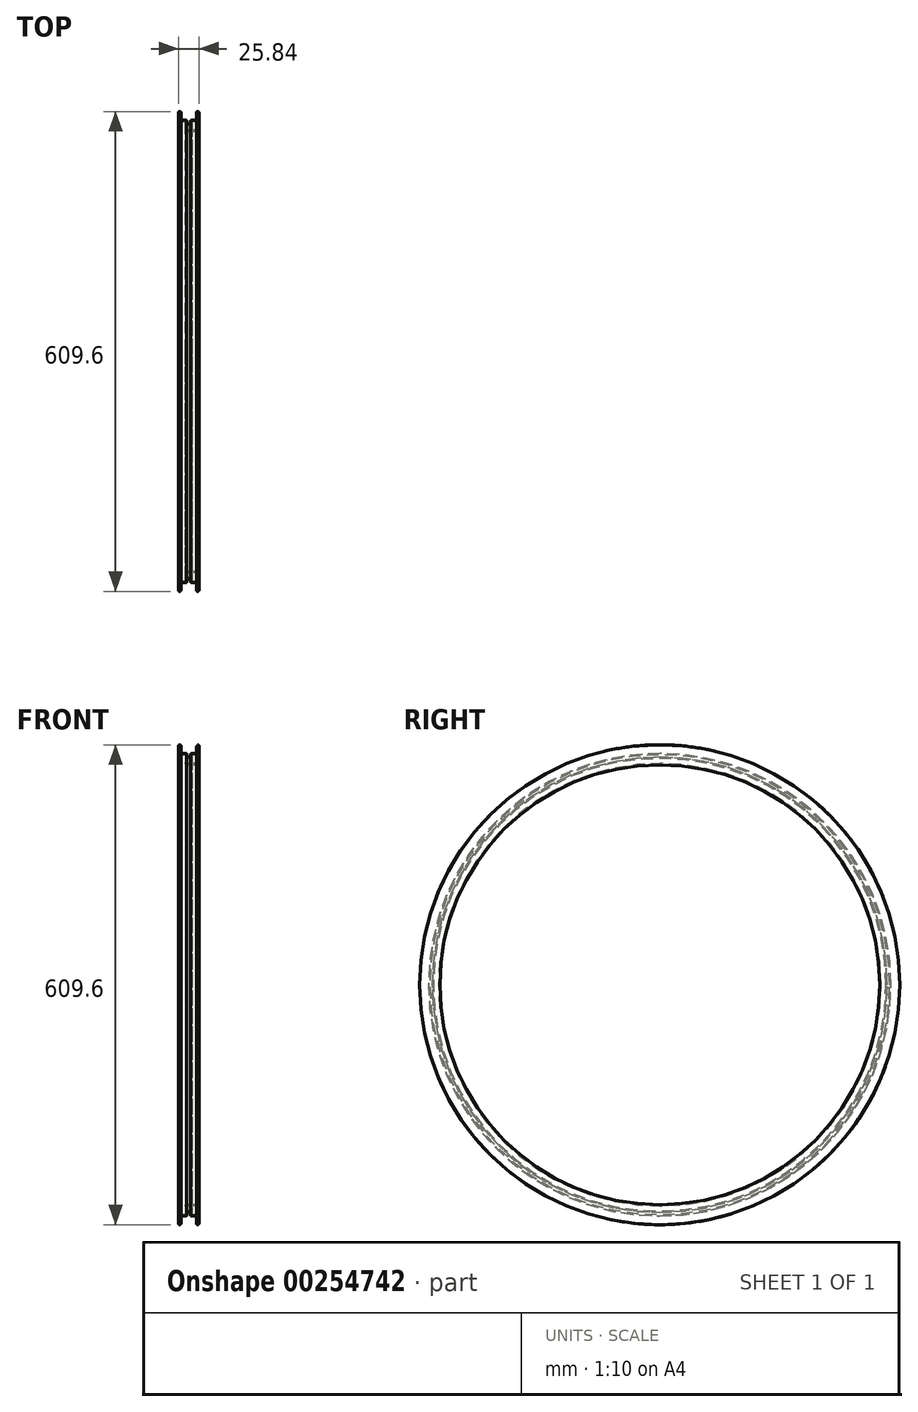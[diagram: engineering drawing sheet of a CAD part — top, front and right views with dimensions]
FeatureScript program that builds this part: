
annotation { "Feature Type Name" : "Feature", "Feature Type Description" : "" }
export const myFeature = defineFeature(function(context is Context, id is Id, definition is map)
    precondition{}
    {
        {
            var Q0;
            Q0=qCreatedBy(makeId("Front.planeOp"),FACE);
            var sketch = newSketch(context, id + "F0", { "sketchPlane" : qUnion([Q0])});
            skLineSegment(sketch, "E0", {"start": v(0, 0) * mm, "end": v(0, 140.25) * mm});
            skLineSegment(sketch, "E1", {"start": v(0, 279.4) * mm, "end": v(10.2, 279.4) * mm});
            skLineSegment(sketch, "E2", {"start": v(0, 280.92) * mm, "end": v(9.48, 280.92) * mm});
            skLineSegment(sketch, "E3", {"start": v(11.5, 304.8) * mm, "end": v(11.5, 304.8) * mm});
            skArc(sketch, "E4", {"start": v(9.48, 280.92) * mm, "mid": v(9.74, 281.03) * mm, "end": v(9.86, 281.28) * mm});
            skArc(sketch, "E5.trimOffspring", {"start": v(10.2, 279.4) * mm, "mid": v(10.97, 279.7) * mm, "end": v(11.33, 280.46) * mm});
            skArc(sketch, "E6", {"start": v(12.92, 303.17) * mm, "mid": v(10.53, 304.53) * mm, "end": v(10.97, 301.82) * mm});
            skLineSegment(sketch, "E7.trimOffspring", {"start": v(12.92, 303.17) * mm, "end": v(11.33, 280.46) * mm});
            skArc(sketch, "E8", {"start": v(11.27, 301.38) * mm, "mid": v(11.2, 301.65) * mm, "end": v(10.97, 301.82) * mm});
            skLineSegment(sketch, "E9.trimOffspring", {"start": v(11.27, 301.38) * mm, "end": v(9.86, 281.28) * mm});
            skLineSegment(sketch, "E10.trimOffspring", {"start": v(11.4, 304.8) * mm, "end": v(11.5, 304.8) * mm});
            skLineSegment(sketch, "E11.trimOffspring", {"start": v(0, 140.25) * mm, "end": v(-5.92, 55.63) * mm});
            skLineSegment(sketch, "E12.trimOffspring", {"start": v(0, 118.4) * mm, "end": v(-11.62, -47.77) * mm});
            skArc(sketch, "E13.MirrorCS", {"start": v(-12.92, 303.17) * mm, "mid": v(-10.53, 304.53) * mm, "end": v(-10.97, 301.82) * mm});
            skLineSegment(sketch, "E14.MirrorCS", {"start": v(-11.27, 301.38) * mm, "end": v(-9.86, 281.28) * mm});
            skLineSegment(sketch, "E15.MirrorCS", {"start": v(-12.92, 303.17) * mm, "end": v(-11.33, 280.46) * mm});
            skArc(sketch, "E16.MirrorCS", {"start": v(-11.27, 301.38) * mm, "mid": v(-11.2, 301.65) * mm, "end": v(-10.97, 301.82) * mm});
            skArc(sketch, "E17.MirrorCS", {"start": v(-10.2, 279.4) * mm, "mid": v(-10.97, 279.7) * mm, "end": v(-11.33, 280.46) * mm});
            skArc(sketch, "E18.MirrorCS", {"start": v(-9.48, 280.92) * mm, "mid": v(-9.74, 281.03) * mm, "end": v(-9.86, 281.28) * mm});
            skLineSegment(sketch, "E19.MirrorCS", {"start": v(0, 280.92) * mm, "end": v(-9.48, 280.92) * mm});
            skLineSegment(sketch, "E20.MirrorCS", {"start": v(0, 279.4) * mm, "end": v(-10.2, 279.4) * mm});
            skLineSegment(sketch, "E21", {"start": v(0, 0) * mm, "end": v(90.13, 0) * mm});
            skLineSegment(sketch, "E22", {"start": v(-10.62, 292.1) * mm, "end": v(-4.06, 292.1) * mm});
            skLineSegment(sketch, "E23", {"start": v(27.13, 292.1) * mm, "end": v(27.13, 293.62) * mm});
            skLineSegment(sketch, "E24", {"start": v(-4.06, 292.1) * mm, "end": v(-4.06, 287.5) * mm});
            skLineSegment(sketch, "E25", {"start": v(-4.06, 287.5) * mm, "end": v(4.06, 287.5) * mm});
            skLineSegment(sketch, "E26", {"start": v(4.06, 287.5) * mm, "end": v(4.06, 292.1) * mm});
            skLineSegment(sketch, "E27", {"start": v(2.54, 293.62) * mm, "end": v(2.54, 289.03) * mm});
            skLineSegment(sketch, "E28", {"start": v(2.54, 289.03) * mm, "end": v(-2.53, 289.03) * mm});
            skLineSegment(sketch, "E29", {"start": v(-2.53, 289.03) * mm, "end": v(-2.53, 293.62) * mm});
            skLineSegment(sketch, "E30.trimOffspring", {"start": v(-2.53, 293.62) * mm, "end": v(-10.73, 293.62) * mm});
            skLineSegment(sketch, "E31.trimOffspring", {"start": v(4.06, 292.1) * mm, "end": v(10.62, 292.1) * mm});
            skLineSegment(sketch, "E32.trimOffspring", {"start": v(10.73, 293.62) * mm, "end": v(2.54, 293.62) * mm});
            skSolve(sketch);
        }
        {
            var Q0;
            Q0 = qSketchRegion(id + "F0", true);
            var Q1;
            Q1=sQuery(id+"F0.wireOp",EDGE,"E21");
            revolve(context, id + "F1", {"entities" : qUnion([Q0]), "axis" : qUnion([Q1]), "revolveType" : RevolveType.FULL});
        }
        {
            var Q0;
            Q0=makeQuery(id+"F1.opRevolve","SWEPT_EDGE",EDGE,{"disambiguationData":[OSD([sQuery(id+"F0.wireOp",EDGE,"E29"),sQuery(id+"F0.wireOp",EDGE,"E30.trimOffspring")])]});
            var Q1;
            Q1=makeQuery(id+"F1.opRevolve","SWEPT_EDGE",EDGE,{"disambiguationData":[OSD([sQuery(id+"F0.wireOp",EDGE,"E28"),sQuery(id+"F0.wireOp",EDGE,"E29")])]});
            var Q2;
            Q2=makeQuery(id+"F1.opRevolve","SWEPT_EDGE",EDGE,{"disambiguationData":[OSD([sQuery(id+"F0.wireOp",EDGE,"E27"),sQuery(id+"F0.wireOp",EDGE,"E32.trimOffspring")])]});
            var Q3;
            Q3=makeQuery(id+"F1.opRevolve","SWEPT_EDGE",EDGE,{"disambiguationData":[OSD([sQuery(id+"F0.wireOp",EDGE,"E27"),sQuery(id+"F0.wireOp",EDGE,"E28")])]});
            var Q4;
            Q4=makeQuery(id+"F1.opRevolve","SWEPT_EDGE",EDGE,{"disambiguationData":[OSD([sQuery(id+"F0.wireOp",EDGE,"E9.trimOffspring"),sQuery(id+"F0.wireOp",EDGE,"E32.trimOffspring")])]});
            var Q5;
            Q5=makeQuery(id+"F1.opRevolve","SWEPT_EDGE",EDGE,{"disambiguationData":[OSD([sQuery(id+"F0.wireOp",EDGE,"E14.MirrorCS"),sQuery(id+"F0.wireOp",EDGE,"E30.trimOffspring")])]});
            fillet(context, id + "F2", {"entities" : qUnion([Q0, Q1, Q2, Q3, Q4, Q5]), "radius" : 0.76 * mm, "tangentPropagation" : true, "allowEdgeOverflow" : false});
        }
    });
